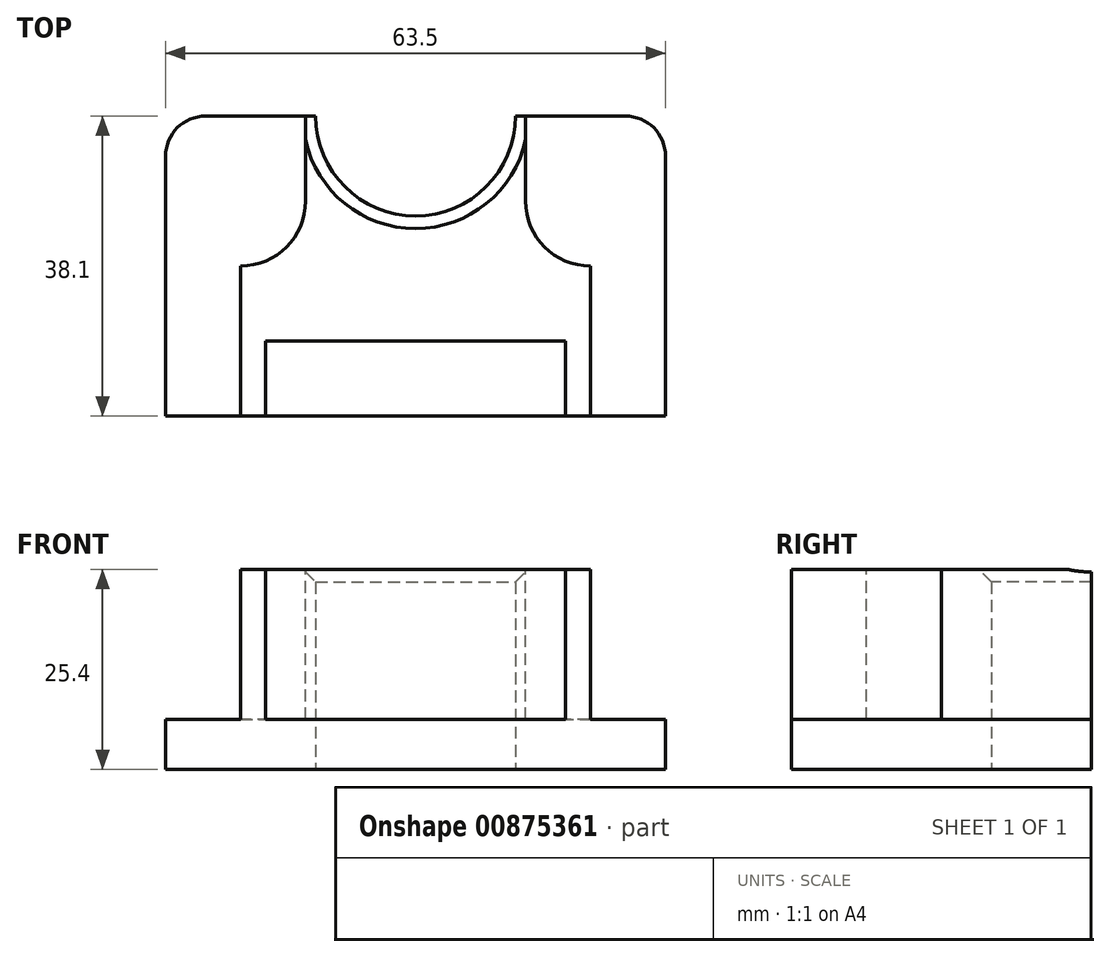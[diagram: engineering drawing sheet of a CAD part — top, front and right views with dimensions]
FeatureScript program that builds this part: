
annotation { "Feature Type Name" : "Feature", "Feature Type Description" : "" }
export const myFeature = defineFeature(function(context is Context, id is Id, definition is map)
    precondition{}
    {
        {
            var Q0;
            Q0=qCreatedBy(makeId("Top.planeOp"),FACE);
            var sketch = newSketch(context, id + "F0", { "sketchPlane" : qUnion([Q0])});
            skCircle(sketch, "E0", {"center": v(-2.64, 0) * mm, "radius": 22.58 * mm});
            skSolve(sketch);
        }
        {
            var Q0;
            Q0=qCreatedBy(makeId("Front.planeOp"),FACE);
            var sketch = newSketch(context, id + "F1", { "sketchPlane" : qUnion([Q0])});
            skLineSegment(sketch, "E1", {"start": v(0, 0) * mm, "end": v(57.7, 65.84) * mm});
            skSolve(sketch);
        }
        {
            var Q0;
            Q0=makeQuery(id+"F0.imprint","IMPRINT",FACE,{"disambiguationData":[TD([[makeQuery(id+"F0.imprint","IMPRINT",EDGE,{"derivedFrom":sQuery(id+"F0.wireOp",EDGE,"E0")}),1.0]])]});
            var Q1;
            Q1=sQuery(id+"F1.wireOp",EDGE,"E1");
            sweep(context, id + "F2", {"profiles" : qUnion([Q0]), "path" : qUnion([Q1])});
        }
        {
            var Q0;
            Q0=makeQuery(id+"F2.opSweep","SWEPT_BODY",BODY,{"disambiguationData":[OSD([sQuery(id+"F0.wireOp",EDGE,"E0"),sQuery(id+"F1.wireOp",EDGE,"E1")])]});
            deleteBodies(context, id + "F3", {"entities" : qUnion([Q0])});
        }
        {
            var Q0;
            Q0=qCreatedBy(makeId("Top.planeOp"),FACE);
            var sketch = newSketch(context, id + "F4", { "sketchPlane" : qUnion([Q0])});
            skLineSegment(sketch, "E2.bottom", {"start": v(31.75, -19.05) * mm, "end": v(-31.75, -19.05) * mm});
            skLineSegment(sketch, "E2.top", {"start": v(31.75, 19.05) * mm, "end": v(-31.75, 19.05) * mm});
            skLineSegment(sketch, "E2.left", {"start": v(31.75, -19.05) * mm, "end": v(31.75, 19.05) * mm});
            skLineSegment(sketch, "E2.right", {"start": v(-31.75, -19.05) * mm, "end": v(-31.75, 19.05) * mm});
            skPoint(sketch, "E2.middle", {"position": v(0, 0) * mm});
            skCircle(sketch, "E3", {"center": v(0, 19.05) * mm, "radius": 12.7 * mm});
            skSolve(sketch);
        }
        {
            var Q0;
            Q0=makeQuery(id+"F4.imprint","IMPRINT",FACE,{"disambiguationData":[TD([[makeQuery(id+"F4.imprint","IMPRINT",EDGE,{"derivedFrom":sQuery(id+"F4.wireOp",EDGE,"E2.bottom")}),-1.0]])]});
            extrude(context, id + "F5", {"entities" : qUnion([Q0]), "depth" : 25.4 * mm, "offsetDistance" : 25.4 * mm});
        }
        {
            var Q0;
            Q0=makeQuery(id+"F5.opExtrude","CAP_FACE",FACE,{"disambiguationData":[OSD([sQuery(id+"F4.wireOp",EDGE,"E2.bottom"),sQuery(id+"F4.wireOp",EDGE,"E2.top"),sQuery(id+"F4.wireOp",EDGE,"E2.left"),sQuery(id+"F4.wireOp",EDGE,"E2.right"),sQuery(id+"F4.wireOp",EDGE,"E3")])],"isStart":false});
            var sketch = newSketch(context, id + "F6", { "sketchPlane" : qUnion([Q0])});
            skLineSegment(sketch, "E4.bottom", {"start": v(31.75, -19.05) * mm, "end": v(22.23, -19.05) * mm});
            skLineSegment(sketch, "E4.top", {"start": v(31.75, 19.05) * mm, "end": v(22.23, 19.05) * mm});
            skLineSegment(sketch, "E4.left", {"start": v(31.75, -19.05) * mm, "end": v(31.75, 19.05) * mm});
            skLineSegment(sketch, "E4.right", {"start": v(22.23, -19.05) * mm, "end": v(22.23, 19.05) * mm});
            skSolve(sketch);
        }
        {
            var Q0;
            Q0=makeQuery(id+"F6.imprint","IMPRINT",FACE,{"disambiguationData":[TD([[makeQuery(id+"F6.imprint","IMPRINT",EDGE,{"derivedFrom":sQuery(id+"F6.wireOp",EDGE,"E4.bottom")}),-1.0]])]});
            extrude(context, id + "F7", {"entities" : qUnion([Q0]), "operationType" : NewBodyOperationType.REMOVE, "oppositeDirection" : true, "depth" : 19.05 * mm, "offsetDistance" : 25.4 * mm});
        }
        {
            var Q0;
            Q0=makeQuery(id+"F5.opExtrude","SWEPT_EDGE",EDGE,{"disambiguationData":[OSD([sQuery(id+"F4.wireOp",EDGE,"E2.top"),sQuery(id+"F4.wireOp",EDGE,"E2.left")])]});
            fillet(context, id + "F8", {"entities" : qUnion([Q0]), "radius" : 5.08 * mm, "tangentPropagation" : true, "allowEdgeOverflow" : false});
        }
        {
            var Q0;
            Q0=makeQuery(id+"F5.opExtrude","CAP_FACE",FACE,{"disambiguationData":[OSD([sQuery(id+"F4.wireOp",EDGE,"E2.bottom"),sQuery(id+"F4.wireOp",EDGE,"E2.top"),sQuery(id+"F4.wireOp",EDGE,"E2.left"),sQuery(id+"F4.wireOp",EDGE,"E2.right"),sQuery(id+"F4.wireOp",EDGE,"E3")])],"isStart":false});
            var sketch = newSketch(context, id + "F9", { "sketchPlane" : qUnion([Q0])});
            skLineSegment(sketch, "E5.bottom", {"start": v(-31.75, -19.05) * mm, "end": v(-22.23, -19.05) * mm});
            skLineSegment(sketch, "E5.top", {"start": v(-31.75, 19.05) * mm, "end": v(-22.23, 19.05) * mm});
            skLineSegment(sketch, "E5.left", {"start": v(-31.75, -19.05) * mm, "end": v(-31.75, 19.05) * mm});
            skLineSegment(sketch, "E5.right", {"start": v(-22.23, -19.05) * mm, "end": v(-22.23, 19.05) * mm});
            skSolve(sketch);
        }
        {
            var Q0;
            Q0=makeQuery(id+"F9.imprint","IMPRINT",FACE,{"disambiguationData":[TD([[makeQuery(id+"F9.imprint","IMPRINT",EDGE,{"derivedFrom":sQuery(id+"F9.wireOp",EDGE,"E5.bottom")}),-1.0]])]});
            extrude(context, id + "F10", {"entities" : qUnion([Q0]), "operationType" : NewBodyOperationType.REMOVE, "oppositeDirection" : true, "depth" : 19.05 * mm, "offsetDistance" : 25.4 * mm});
        }
        {
            var Q0;
            Q0=makeQuery(id+"F5.opExtrude","CAP_FACE",FACE,{"disambiguationData":[OSD([sQuery(id+"F4.wireOp",EDGE,"E2.bottom"),sQuery(id+"F4.wireOp",EDGE,"E2.top"),sQuery(id+"F4.wireOp",EDGE,"E2.left"),sQuery(id+"F4.wireOp",EDGE,"E2.right"),sQuery(id+"F4.wireOp",EDGE,"E3")])],"isStart":false});
            var sketch = newSketch(context, id + "F11", { "sketchPlane" : qUnion([Q0])});
            skLineSegment(sketch, "E6.bottom", {"start": v(-19.05, -28.57) * mm, "end": v(19.05, -28.57) * mm});
            skLineSegment(sketch, "E6.top", {"start": v(-19.05, -9.52) * mm, "end": v(19.05, -9.52) * mm});
            skLineSegment(sketch, "E6.left", {"start": v(-19.05, -28.57) * mm, "end": v(-19.05, -9.52) * mm});
            skLineSegment(sketch, "E6.right", {"start": v(19.05, -28.57) * mm, "end": v(19.05, -9.52) * mm});
            skPoint(sketch, "E6.middle", {"position": v(0, -19.05) * mm});
            skSolve(sketch);
        }
        {
            var Q0;
            {var subQ0=sQuery(id+"F11.wireOp",EDGE,"E6.top");Q0=makeQuery(id+"F11.imprint","IMPRINT",FACE,{"disambiguationData":[TD([[makeQuery(id+"F11.imprint","IMPRINT",EDGE,{"derivedFrom":subQ0}),-1.0]])]});}
            extrude(context, id + "F12", {"entities" : qUnion([Q0]), "operationType" : NewBodyOperationType.REMOVE, "oppositeDirection" : true, "depth" : 19.05 * mm, "offsetDistance" : 25.4 * mm});
        }
        {
            var Q0;
            Q0=makeQuery(id+"F5.opExtrude","CAP_FACE",FACE,{"disambiguationData":[OSD([sQuery(id+"F4.wireOp",EDGE,"E2.bottom"),sQuery(id+"F4.wireOp",EDGE,"E2.top"),sQuery(id+"F4.wireOp",EDGE,"E2.left"),sQuery(id+"F4.wireOp",EDGE,"E2.right"),sQuery(id+"F4.wireOp",EDGE,"E3")])],"isStart":false});
            var sketch = newSketch(context, id + "F13", { "sketchPlane" : qUnion([Q0])});
            skLineSegment(sketch, "E7.bottom", {"start": v(-22.23, 19.05) * mm, "end": v(-13.97, 19.05) * mm});
            skLineSegment(sketch, "E7.top", {"start": v(-22.23, 0) * mm, "end": v(-13.97, 0) * mm});
            skLineSegment(sketch, "E7.left", {"start": v(-22.23, 19.05) * mm, "end": v(-22.23, 0) * mm});
            skLineSegment(sketch, "E7.right", {"start": v(-13.97, 19.05) * mm, "end": v(-13.97, 0) * mm});
            skLineSegment(sketch, "E8.bottom", {"start": v(22.23, 19.05) * mm, "end": v(13.97, 19.05) * mm});
            skLineSegment(sketch, "E8.top", {"start": v(22.23, 0) * mm, "end": v(13.97, 0) * mm});
            skLineSegment(sketch, "E8.left", {"start": v(22.23, 19.05) * mm, "end": v(22.23, 0) * mm});
            skLineSegment(sketch, "E8.right", {"start": v(13.97, 19.05) * mm, "end": v(13.97, 0) * mm});
            skSolve(sketch);
        }
        {
            var Q0;
            Q0=makeQuery(id+"F5.opExtrude","SWEPT_EDGE",EDGE,{"disambiguationData":[OSD([sQuery(id+"F4.wireOp",EDGE,"E2.top"),sQuery(id+"F4.wireOp",EDGE,"E2.right")])]});
            fillet(context, id + "F14", {"entities" : qUnion([Q0]), "radius" : 5.08 * mm, "tangentPropagation" : true, "allowEdgeOverflow" : false});
        }
        {
            var Q0;
            Q0=makeQuery(id+"F13.imprint","IMPRINT",FACE,{"disambiguationData":[TD([[makeQuery(id+"F13.imprint","IMPRINT",EDGE,{"derivedFrom":sQuery(id+"F13.wireOp",EDGE,"E7.bottom")}),1.0]])]});
            var Q1;
            Q1=makeQuery(id+"F13.imprint","IMPRINT",FACE,{"disambiguationData":[TD([[makeQuery(id+"F13.imprint","IMPRINT",EDGE,{"derivedFrom":sQuery(id+"F13.wireOp",EDGE,"E8.bottom")}),1.0]])]});
            extrude(context, id + "F15", {"entities" : qUnion([Q0, Q1]), "operationType" : NewBodyOperationType.REMOVE, "oppositeDirection" : true, "depth" : 19.05 * mm, "offsetDistance" : 25.4 * mm});
        }
        {
            var Q0;
            Q0=makeQuery(id+"F15.boolean.opBoolean","COPY",EDGE,{"derivedFrom":makeQuery(id+"F15.opExtrude","SWEPT_EDGE",EDGE,{"disambiguationData":[OSD([sQuery(id+"F13.wireOp",EDGE,"E7.top"),sQuery(id+"F13.wireOp",EDGE,"E7.right")])]})});
            var Q1;
            Q1=makeQuery(id+"F15.boolean.opBoolean","COPY",EDGE,{"derivedFrom":makeQuery(id+"F15.opExtrude","SWEPT_EDGE",EDGE,{"disambiguationData":[OSD([sQuery(id+"F13.wireOp",EDGE,"E8.top"),sQuery(id+"F13.wireOp",EDGE,"E8.right")])]})});
            fillet(context, id + "F16", {"entities" : qUnion([Q0, Q1]), "radius" : 8.25 * mm, "tangentPropagation" : true, "allowEdgeOverflow" : false});
        }
        {
            var Q0;
            Q0=makeQuery(id+"F5.opExtrude","CAP_EDGE",EDGE,{"disambiguationData":[OSD([sQuery(id+"F4.wireOp",EDGE,"E3")])],"isStart":false});
            var Q1;
            Q1=makeQuery(id+"F12.boolean.opBoolean","COPY",EDGE,{"derivedFrom":makeQuery(id+"F12.opExtrude","CAP_EDGE",EDGE,{"disambiguationData":[OSD([sQuery(id+"F11.wireOp",EDGE,"E6.top")])],"isStart":true})});
            var Q2;
            Q2=makeQuery(id+"F12.boolean.opBoolean","COPY",EDGE,{"derivedFrom":makeQuery(id+"F12.opExtrude","CAP_EDGE",EDGE,{"disambiguationData":[OSD([sQuery(id+"F11.wireOp",EDGE,"E6.left")])],"isStart":true})});
            var Q3;
            Q3=makeQuery(id+"F12.boolean.opBoolean","COPY",EDGE,{"derivedFrom":makeQuery(id+"F12.opExtrude","CAP_EDGE",EDGE,{"disambiguationData":[OSD([sQuery(id+"F11.wireOp",EDGE,"E6.right")])],"isStart":true})});
            chamfer(context, id + "F17", {"entities" : qUnion([Q0, Q1, Q2, Q3]), "width" : 1.59 * mm, "tangentPropagation" : true});
        }
    });
